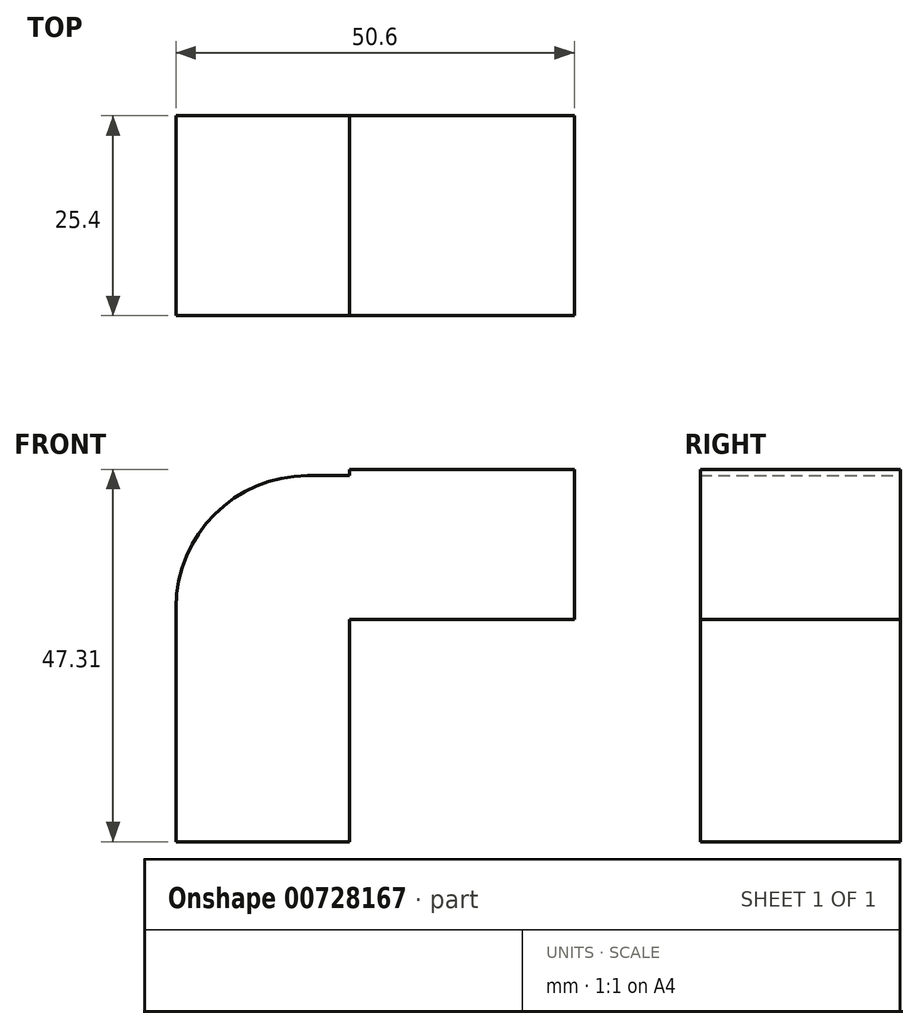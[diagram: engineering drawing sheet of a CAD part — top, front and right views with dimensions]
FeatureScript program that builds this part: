
annotation { "Feature Type Name" : "Feature", "Feature Type Description" : "" }
export const myFeature = defineFeature(function(context is Context, id is Id, definition is map)
    precondition{}
    {
        {
            var Q0;
            Q0=qCreatedBy(makeId("Front.planeOp"),FACE);
            var sketch = newSketch(context, id + "F0", { "sketchPlane" : qUnion([Q0])});
            skLineSegment(sketch, "E0.bottom", {"start": v(25.4, 12.7) * mm, "end": v(-25.4, 12.7) * mm});
            skLineSegment(sketch, "E0.top", {"start": v(25.4, -12.7) * mm, "end": v(-25.4, -12.7) * mm});
            skLineSegment(sketch, "E0.left", {"start": v(25.4, 12.7) * mm, "end": v(25.4, -12.7) * mm});
            skLineSegment(sketch, "E0.right", {"start": v(-25.4, 12.7) * mm, "end": v(-25.4, -12.7) * mm});
            skPoint(sketch, "E0.middle", {"position": v(0, 0) * mm});
            skLineSegment(sketch, "E1.bottom", {"start": v(53.34, 40.96) * mm, "end": v(24.77, 40.96) * mm});
            skLineSegment(sketch, "E1.top", {"start": v(53.34, 60.01) * mm, "end": v(24.77, 60.01) * mm});
            skLineSegment(sketch, "E1.left", {"start": v(53.34, 40.96) * mm, "end": v(53.34, 60.01) * mm});
            skLineSegment(sketch, "E1.right", {"start": v(24.77, 40.96) * mm, "end": v(24.77, 60.01) * mm});
            skPoint(sketch, "E1.middle", {"position": v(39.06, 50.49) * mm});
            skLineSegment(sketch, "E2", {"start": v(24.77, 40.96) * mm, "end": v(24.77, 12.7) * mm});
            skLineSegment(sketch, "E3", {"start": v(2.74, 12.7) * mm, "end": v(2.74, 42.47) * mm});
            skArc(sketch, "E4", {"start": v(2.74, 42.47) * mm, "mid": v(7.64, 54.3) * mm, "end": v(19.47, 59.2) * mm});
            skLineSegment(sketch, "E5", {"start": v(19.47, 59.2) * mm, "end": v(24.77, 59.2) * mm});
            skLineSegment(sketch, "E6.0", {"start": v(19.47, 52.84) * mm, "end": v(24.77, 52.84) * mm});
            skArc(sketch, "E6.1", {"start": v(9.1, 42.47) * mm, "mid": v(12.13, 49.8) * mm, "end": v(19.47, 52.84) * mm});
            skLineSegment(sketch, "E6.2", {"start": v(9.1, 12.7) * mm, "end": v(9.1, 42.47) * mm});
            skSolve(sketch);
        }
        {
            var Q0;
            {var subQ1=sQuery(id+"F0.wireOp",EDGE,"E1.bottom");Q0=makeQuery(id+"F0.imprint","IMPRINT",FACE,{"disambiguationData":[TD([[makeQuery(id+"F0.imprint","IMPRINT",EDGE,{"derivedFrom":subQ1}),-1.0]])]});}
            var Q1;
            {var subQ1=sQuery(id+"F0.wireOp",EDGE,"E2");Q1=makeQuery(id+"F0.imprint","IMPRINT",FACE,{"disambiguationData":[TD([[makeQuery(id+"F0.imprint","IMPRINT",EDGE,{"derivedFrom":subQ1}),-1.0]])]});}
            var Q2;
            {var subQ0=sQuery(id+"F0.wireOp",EDGE,"E3");Q2=makeQuery(id+"F0.imprint","IMPRINT",FACE,{"disambiguationData":[TD([[makeQuery(id+"F0.imprint","IMPRINT",EDGE,{"derivedFrom":subQ0}),-1.0]])]});}
            extrude(context, id + "F1", {"entities" : qUnion([Q0, Q1, Q2]), "depth" : 25.4 * mm, "offsetDistance" : 25.4 * mm});
        }
    });
